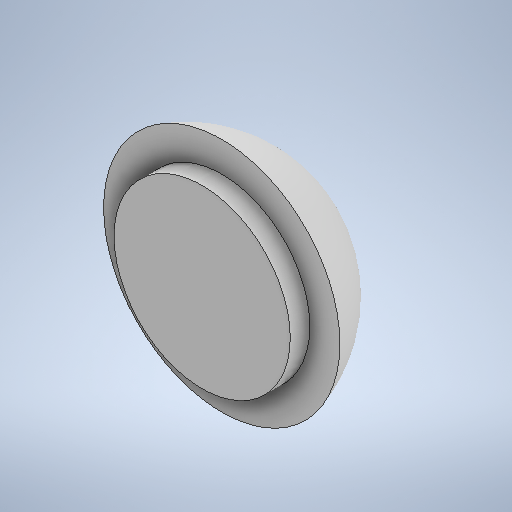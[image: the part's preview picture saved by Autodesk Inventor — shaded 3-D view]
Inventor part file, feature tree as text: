
AUTODESK INVENTOR PART (.ipt)
format: ipt  version: 2025.1 (Build 291241000, 241)  size: 261,120 bytes
history: native  units: mm
features: revolve x1, sketch x1
ambient origin geometry x8: Origin, YZ Plane, XZ Plane, XY Plane, X Axis, Y Axis, Z Axis, Center Point
bodies: Solid1 (feature_tree)
feature tree (2):
  revolve  "Revolution1"  [1 undecoded]
  sketch  "Sketch1"  dims[d0=5.5mm d1=1.0mm d2=6.3mm d3=9.0mm d4=90.0deg]
note: 1 required parameter value undecoded (feature->parameter linkage not recoverable at this tier; creation-order binding heuristic only, values carry confidence <= 0.55)
